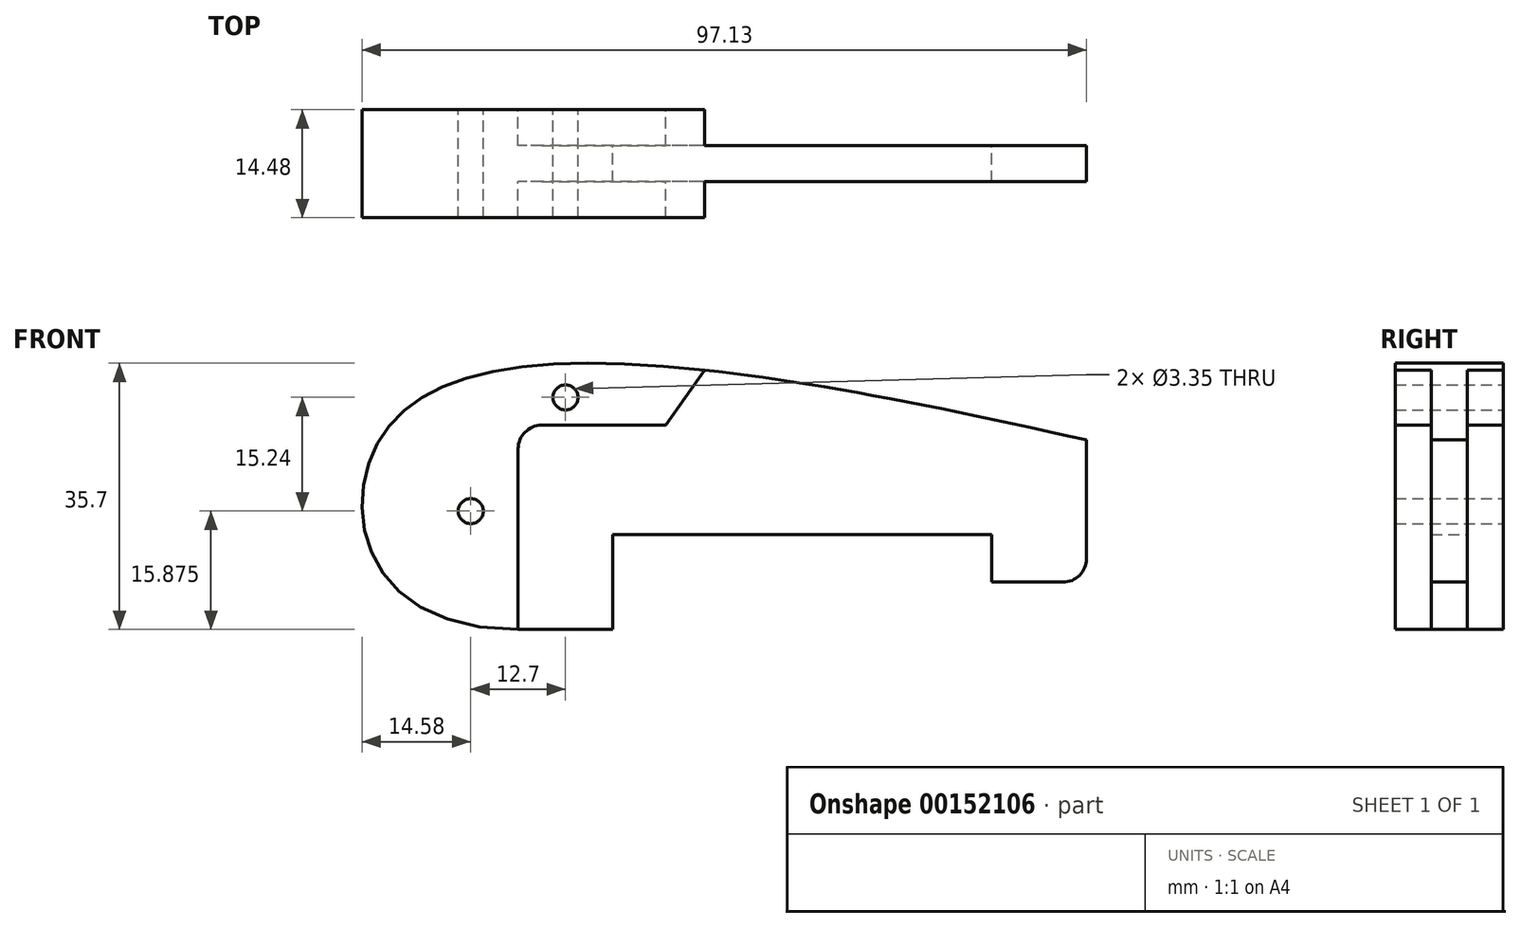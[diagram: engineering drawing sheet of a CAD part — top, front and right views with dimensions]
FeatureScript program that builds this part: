
annotation { "Feature Type Name" : "Feature", "Feature Type Description" : "" }
export const myFeature = defineFeature(function(context is Context, id is Id, definition is map)
    precondition{}
    {
        {
            var Q0;
            Q0=qCreatedBy(makeId("Front.planeOp"),FACE);
            var sketch = newSketch(context, id + "F0", { "sketchPlane" : qUnion([Q0])});
            skLineSegment(sketch, "E0", {"start": v(0, 0) * mm, "end": v(0, 25.4) * mm});
            skLineSegment(sketch, "E1", {"start": v(0, 25.4) * mm, "end": v(76.2, 25.4) * mm});
            skLineSegment(sketch, "E2", {"start": v(76.2, 25.4) * mm, "end": v(76.2, 9.52) * mm});
            skLineSegment(sketch, "E3", {"start": v(73.03, 6.35) * mm, "end": v(63.5, 6.35) * mm});
            skLineSegment(sketch, "E4", {"start": v(63.5, 6.35) * mm, "end": v(63.5, 12.7) * mm});
            skLineSegment(sketch, "E5", {"start": v(63.5, 12.7) * mm, "end": v(12.7, 12.7) * mm});
            skLineSegment(sketch, "E6", {"start": v(12.7, 12.7) * mm, "end": v(12.7, 0) * mm});
            skLineSegment(sketch, "E7", {"start": v(12.7, 0) * mm, "end": v(0, 0) * mm});
            skFitSpline(sketch, "E8", {"points": [v(76.2, 25.4) * mm, v(-18.6, 25.4) * mm, v(0, 0) * mm], "startDerivative": vector(-234.27, 53.07) * mm, "endDerivative": vector(170.2, 0) * mm});
            skPoint(sketch, "E9.visualSharp", {"position": v(76.2, 6.35) * mm});
            skArc(sketch, "E9.filletArc", {"start": v(73.03, 6.35) * mm, "mid": v(75.27, 7.28) * mm, "end": v(76.2, 9.52) * mm});
            skCircle(sketch, "E10", {"center": v(-6.35, 15.88) * mm, "radius": 1.68 * mm});
            skCircle(sketch, "E11", {"center": v(6.35, 31.12) * mm, "radius": 1.68 * mm});
            skPoint(sketch, "E12", {"position": v(6.35, 0) * mm});
            skSolve(sketch);
        }
        {
            var Q0;
            Q0=makeQuery(id+"F0.imprint","IMPRINT",FACE,{"disambiguationData":[TD([[makeQuery(id+"F0.imprint","IMPRINT",EDGE,{"derivedFrom":sQuery(id+"F0.wireOp",EDGE,"E0")}),-1.0]])]});
            var Q1;
            Q1=makeQuery(id+"F0.imprint","IMPRINT",FACE,{"disambiguationData":[TD([[makeQuery(id+"F0.imprint","IMPRINT",EDGE,{"derivedFrom":sQuery(id+"F0.wireOp",EDGE,"E1")}),1.0]])]});
            extrude(context, id + "F1", {"entities" : qUnion([Q0, Q1]), "depth" : 4.83 * mm});
        }
        {
            var Q0;
            Q0=makeQuery(id+"F1.opExtrude","CAP_FACE",FACE,{"disambiguationData":[OSD([sQuery(id+"F0.wireOp",EDGE,"E2"),sQuery(id+"F0.wireOp",EDGE,"E3"),sQuery(id+"F0.wireOp",EDGE,"E4"),sQuery(id+"F0.wireOp",EDGE,"E5"),sQuery(id+"F0.wireOp",EDGE,"E6"),sQuery(id+"F0.wireOp",EDGE,"E7"),sQuery(id+"F0.wireOp",EDGE,"E8"),sQuery(id+"F0.wireOp",EDGE,"E9.filletArc")])],"isStart":false});
            var sketch = newSketch(context, id + "F2", { "sketchPlane" : qUnion([Q0])});
            skLineSegment(sketch, "E13", {"start": v(19.77, 27.39) * mm, "end": v(3.18, 27.39) * mm});
            skLineSegment(sketch, "E14", {"start": v(0, 24.21) * mm, "end": v(0, 0) * mm});
            skPoint(sketch, "E15.visualSharp", {"position": v(0, 27.39) * mm});
            skArc(sketch, "E15.filletArc", {"start": v(3.18, 27.39) * mm, "mid": v(0.93, 26.46) * mm, "end": v(0, 24.21) * mm});
            skLineSegment(sketch, "E16", {"start": v(19.77, 27.39) * mm, "end": v(25, 34.77) * mm});
            skSolve(sketch);
        }
        {
            var Q0;
            Q0=makeQuery(id+"F2.imprint","IMPRINT",FACE,{"disambiguationData":[TD([[makeQuery(id+"F2.imprint","IMPRINT",EDGE,{"derivedFrom":sQuery(id+"F2.wireOp",EDGE,"E13")}),-1.0]])]});
            extrude(context, id + "F3", {"entities" : qUnion([Q0]), "operationType" : NewBodyOperationType.ADD, "depth" : 4.83 * mm, "hasSecondDirection" : true, "secondDirectionOppositeDirection" : true, "secondDirectionDepth" : 9.65 * mm});
        }
    });
